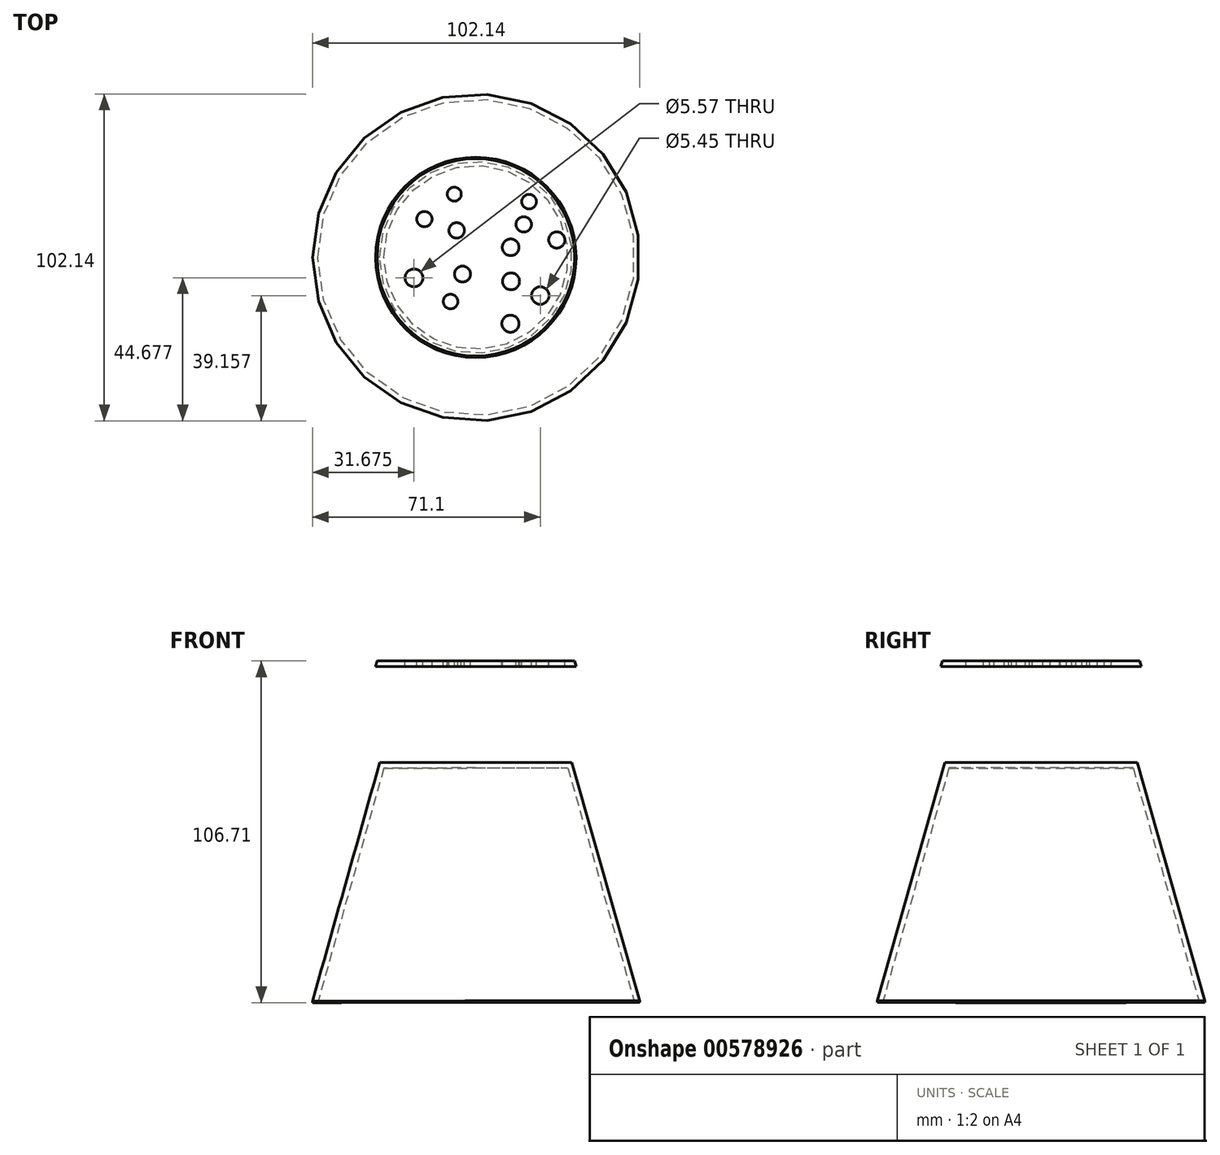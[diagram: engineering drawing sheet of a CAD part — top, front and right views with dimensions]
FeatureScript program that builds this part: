
annotation { "Feature Type Name" : "Feature", "Feature Type Description" : "" }
export const myFeature = defineFeature(function(context is Context, id is Id, definition is map)
    precondition{}
    {
        {
            var Q0;
            Q0=qCreatedBy(makeId("Front.planeOp"),FACE);
            var sketch = newSketch(context, id + "F0", { "sketchPlane" : qUnion([Q0])});
            skLineSegment(sketch, "E0.0", {"start": v(-30, -0.05) * mm, "end": v(-50.97, -74.54) * mm});
            skLineSegment(sketch, "E1.0", {"start": v(-28.71, -1.75) * mm, "end": v(-49.34, -75) * mm});
            skLineSegment(sketch, "E2", {"start": v(-49.34, -75) * mm, "end": v(-50.97, -75) * mm});
            skLineSegment(sketch, "E3", {"start": v(-50.97, -75) * mm, "end": v(-50.97, -74.54) * mm});
            skLineSegment(sketch, "E4", {"start": v(0, 0) * mm, "end": v(-30, -0.05) * mm});
            skLineSegment(sketch, "E5.0", {"start": v(0, -1.7) * mm, "end": v(-28.71, -1.75) * mm});
            skLineSegment(sketch, "E6", {"start": v(0, -1.7) * mm, "end": v(0, 0) * mm});
            skPoint(sketch, "E7.end.orphan", {"position": v(-30, -1.75) * mm});
            skPoint(sketch, "E8.end.orphan", {"position": v(-29.35, -1.75) * mm});
            skLineSegment(sketch, "E9", {"start": v(-30.82, -9.25) * mm, "end": v(-31.3, -10.93) * mm});
            skLineSegment(sketch, "E10", {"start": v(0, 31.7) * mm, "end": v(-30.82, 31.7) * mm});
            skLineSegment(sketch, "E11", {"start": v(-30.82, 31.7) * mm, "end": v(-31.3, 30.02) * mm});
            skLineSegment(sketch, "E12", {"start": v(-31.3, 30.02) * mm, "end": v(0, 30.02) * mm});
            skLineSegment(sketch, "E13", {"start": v(0, 30.02) * mm, "end": v(0, 31.7) * mm});
            skPoint(sketch, "E14.end.orphan", {"position": v(0, -9.25) * mm});
            skPoint(sketch, "E14.start.orphan", {"position": v(0, -10.93) * mm});
            skSolve(sketch);
        }
        {
            var Q0;
            Q0=makeQuery(id+"F0.imprint","IMPRINT",FACE,{"disambiguationData":[TD([[makeQuery(id+"F0.imprint","IMPRINT",EDGE,{"derivedFrom":sQuery(id+"F0.wireOp",EDGE,"E0.0")}),1.0]])]});
            var Q1;
            Q1=sQuery(id+"F0.wireOp",EDGE,"E6");
            revolve(context, id + "F1", {"entities" : qUnion([Q0]), "axis" : qUnion([Q1]), "revolveType" : RevolveType.FULL});
        }
        {
            var Q0;
            Q0=makeQuery(id+"F0.imprint","IMPRINT",FACE,{"disambiguationData":[TD([[makeQuery(id+"F0.imprint","IMPRINT",EDGE,{"derivedFrom":sQuery(id+"F0.wireOp",EDGE,"E10")}),1.0]])]});
            var Q1;
            Q1=sQuery(id+"F0.wireOp",EDGE,"E13");
            revolve(context, id + "F2", {"entities" : qUnion([Q0]), "axis" : qUnion([Q1]), "revolveType" : RevolveType.FULL});
        }
        {
            var Q0;
            Q0=makeQuery(id+"F2.opRevolve","SWEPT_FACE",FACE,{"disambiguationData":[OSD([sQuery(id+"F0.wireOp",EDGE,"E10")])]});
            var sketch = newSketch(context, id + "F3", { "sketchPlane" : qUnion([Q0])});
            skCircle(sketch, "E15", {"center": v(-6.72, 19.75) * mm, "radius": 2.18 * mm});
            skCircle(sketch, "E16", {"center": v(-16.04, 11.97) * mm, "radius": 2.39 * mm});
            skCircle(sketch, "E17", {"center": v(-5.98, 8.44) * mm, "radius": 2.42 * mm});
            skCircle(sketch, "E18", {"center": v(-19.3, -6.4) * mm, "radius": 2.79 * mm});
            skCircle(sketch, "E19", {"center": v(-7.89, -13.78) * mm, "radius": 2.27 * mm});
            skCircle(sketch, "E20", {"center": v(-4.15, -5.2) * mm, "radius": 2.49 * mm});
            skCircle(sketch, "E21", {"center": v(10.82, -20.7) * mm, "radius": 2.66 * mm});
            skCircle(sketch, "E22", {"center": v(20.13, -11.91) * mm, "radius": 2.72 * mm});
            skCircle(sketch, "E23", {"center": v(10.88, 3.16) * mm, "radius": 2.6 * mm});
            skCircle(sketch, "E24", {"center": v(14.96, 10.32) * mm, "radius": 2.4 * mm});
            skCircle(sketch, "E25", {"center": v(25.26, 5.45) * mm, "radius": 2.53 * mm});
            skCircle(sketch, "E26", {"center": v(16.63, 17.4) * mm, "radius": 2.28 * mm});
            skCircle(sketch, "E27", {"center": v(11, -7.48) * mm, "radius": 2.64 * mm});
            skCircle(sketch, "E28", {"center": v(-6.36, -22.91) * mm, "radius": 2.63 * mm});
            skSolve(sketch);
        }
        {
            var Q0;
            Q0=makeQuery(id+"F3.imprint","IMPRINT",FACE,{"disambiguationData":[TD([[makeQuery(id+"F3.imprint","IMPRINT",EDGE,{"derivedFrom":sQuery(id+"F3.wireOp",EDGE,"E19")}),1.0]])]});
            var Q1;
            Q1=makeQuery(id+"F3.imprint","IMPRINT",FACE,{"disambiguationData":[TD([[makeQuery(id+"F3.imprint","IMPRINT",EDGE,{"derivedFrom":sQuery(id+"F3.wireOp",EDGE,"E15")}),1.0]])]});
            var Q2;
            Q2=makeQuery(id+"F3.imprint","IMPRINT",FACE,{"disambiguationData":[TD([[makeQuery(id+"F3.imprint","IMPRINT",EDGE,{"derivedFrom":sQuery(id+"F3.wireOp",EDGE,"E26")}),1.0]])]});
            var Q3;
            Q3=makeQuery(id+"F3.imprint","IMPRINT",FACE,{"disambiguationData":[TD([[makeQuery(id+"F3.imprint","IMPRINT",EDGE,{"derivedFrom":sQuery(id+"F3.wireOp",EDGE,"E27")}),1.0]])]});
            var Q4;
            Q4=makeQuery(id+"F3.imprint","IMPRINT",FACE,{"disambiguationData":[TD([[makeQuery(id+"F3.imprint","IMPRINT",EDGE,{"derivedFrom":sQuery(id+"F3.wireOp",EDGE,"E22")}),1.0]])]});
            var Q5;
            Q5=makeQuery(id+"F3.imprint","IMPRINT",FACE,{"disambiguationData":[TD([[makeQuery(id+"F3.imprint","IMPRINT",EDGE,{"derivedFrom":sQuery(id+"F3.wireOp",EDGE,"E21")}),1.0]])]});
            var Q6;
            Q6=makeQuery(id+"F3.imprint","IMPRINT",FACE,{"disambiguationData":[TD([[makeQuery(id+"F3.imprint","IMPRINT",EDGE,{"derivedFrom":sQuery(id+"F3.wireOp",EDGE,"E23")}),1.0]])]});
            var Q7;
            Q7=makeQuery(id+"F3.imprint","IMPRINT",FACE,{"disambiguationData":[TD([[makeQuery(id+"F3.imprint","IMPRINT",EDGE,{"derivedFrom":sQuery(id+"F3.wireOp",EDGE,"E24")}),1.0]])]});
            var Q8;
            Q8=makeQuery(id+"F3.imprint","IMPRINT",FACE,{"disambiguationData":[TD([[makeQuery(id+"F3.imprint","IMPRINT",EDGE,{"derivedFrom":sQuery(id+"F3.wireOp",EDGE,"E25")}),1.0]])]});
            var Q9;
            Q9=makeQuery(id+"F3.imprint","IMPRINT",FACE,{"disambiguationData":[TD([[makeQuery(id+"F3.imprint","IMPRINT",EDGE,{"derivedFrom":sQuery(id+"F3.wireOp",EDGE,"E17")}),1.0]])]});
            var Q10;
            Q10=makeQuery(id+"F3.imprint","IMPRINT",FACE,{"disambiguationData":[TD([[makeQuery(id+"F3.imprint","IMPRINT",EDGE,{"derivedFrom":sQuery(id+"F3.wireOp",EDGE,"E16")}),1.0]])]});
            var Q11;
            Q11=makeQuery(id+"F3.imprint","IMPRINT",FACE,{"disambiguationData":[TD([[makeQuery(id+"F3.imprint","IMPRINT",EDGE,{"derivedFrom":sQuery(id+"F3.wireOp",EDGE,"E20")}),1.0]])]});
            var Q12;
            Q12=makeQuery(id+"F3.imprint","IMPRINT",FACE,{"disambiguationData":[TD([[makeQuery(id+"F3.imprint","IMPRINT",EDGE,{"derivedFrom":sQuery(id+"F3.wireOp",EDGE,"E18")}),1.0]])]});
            extrude(context, id + "F4", {"entities" : qUnion([Q0, Q1, Q2, Q3, Q4, Q5, Q6, Q7, Q8, Q9, Q10, Q11, Q12]), "operationType" : NewBodyOperationType.REMOVE, "oppositeDirection" : true, "depth" : 2.1 * mm, "offsetDistance" : 25 * mm});
        }
    });
